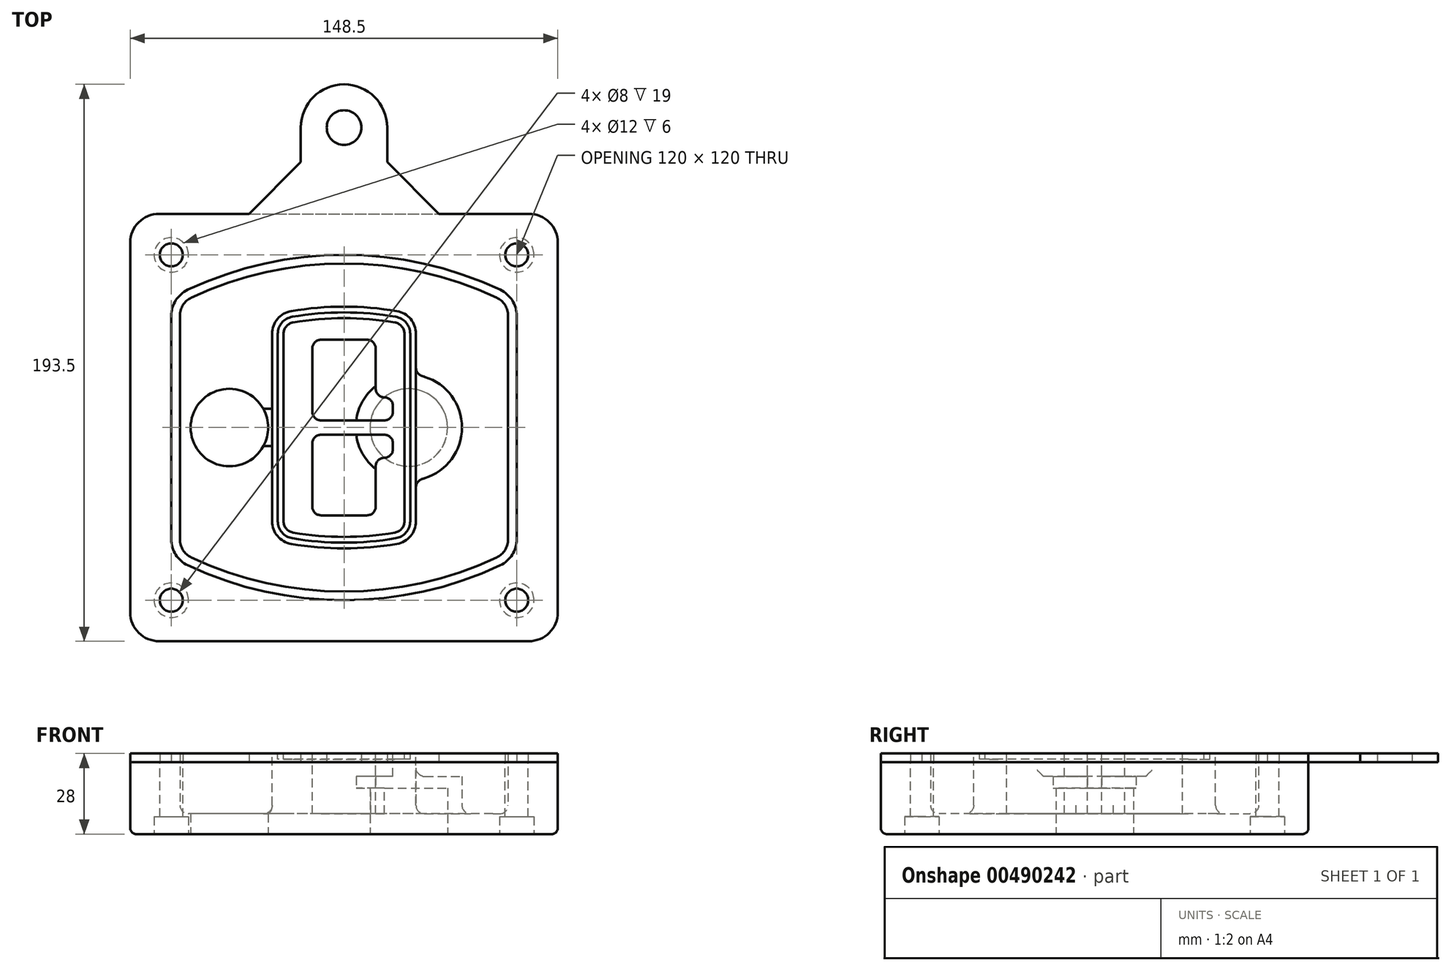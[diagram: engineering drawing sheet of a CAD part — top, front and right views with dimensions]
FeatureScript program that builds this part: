
annotation { "Feature Type Name" : "Feature", "Feature Type Description" : "" }
export const myFeature = defineFeature(function(context is Context, id is Id, definition is map)
    precondition{}
    {
        {
            var Q0;
            Q0=qCreatedBy(makeId("Top.planeOp"),FACE);
            var sketch = newSketch(context, id + "F0", { "sketchPlane" : qUnion([Q0])});
            skPoint(sketch, "E0.rect.middle", {"position": v(0, 0) * mm});
            skLineSegment(sketch, "E1.bottom", {"start": v(-64.25, -74.25) * mm, "end": v(64.25, -74.25) * mm});
            skLineSegment(sketch, "E1.top", {"start": v(-64.25, 74.25) * mm, "end": v(64.25, 74.25) * mm});
            skLineSegment(sketch, "E1.left", {"start": v(-74.25, -64.25) * mm, "end": v(-74.25, 64.25) * mm});
            skLineSegment(sketch, "E1.right", {"start": v(74.25, -64.25) * mm, "end": v(74.25, 64.25) * mm});
            skLineSegment(sketch, "E2", {"start": v(-74.25, 74.25) * mm, "end": v(74.25, -74.25) * mm, "construction": true});
            skLineSegment(sketch, "E3", {"start": v(74.25, 74.25) * mm, "end": v(-74.25, -74.25) * mm, "construction": true});
            skCircle(sketch, "E4", {"center": v(-60, 60) * mm, "radius": 4 * mm});
            skCircle(sketch, "E5", {"center": v(60, 60) * mm, "radius": 4 * mm});
            skCircle(sketch, "E6", {"center": v(60, -60) * mm, "radius": 4 * mm});
            skCircle(sketch, "E7", {"center": v(-60, -60) * mm, "radius": 4 * mm});
            skLineSegment(sketch, "E8", {"start": v(-60, 60) * mm, "end": v(60, 60) * mm, "construction": true});
            skLineSegment(sketch, "E9", {"start": v(60, 60) * mm, "end": v(60, -60) * mm, "construction": true});
            skLineSegment(sketch, "E10", {"start": v(60, -60) * mm, "end": v(-60, -60) * mm, "construction": true});
            skLineSegment(sketch, "E11", {"start": v(-60, -60) * mm, "end": v(-60, 60) * mm, "construction": true});
            skLineSegment(sketch, "E12", {"start": v(-60, 38.83) * mm, "end": v(-60, -38.83) * mm});
            skLineSegment(sketch, "E13", {"start": v(60, 38.83) * mm, "end": v(60, -38.83) * mm});
            skArc(sketch, "E14", {"start": v(54.26, 47.88) * mm, "mid": v(0, 60) * mm, "end": v(-54.26, 47.88) * mm});
            skArc(sketch, "E15", {"start": v(-54.26, -47.88) * mm, "mid": v(0, -60) * mm, "end": v(54.26, -47.88) * mm});
            skLineSegment(sketch, "E16", {"start": v(-60, 0) * mm, "end": v(60, 0) * mm, "construction": true});
            skPoint(sketch, "E17.visualSharp", {"position": v(-60, -45) * mm});
            skArc(sketch, "E17.filletArc", {"start": v(-60, -38.83) * mm, "mid": v(-58.44, -44.2) * mm, "end": v(-54.26, -47.88) * mm});
            skPoint(sketch, "E18.visualSharp", {"position": v(-60, 45) * mm});
            skArc(sketch, "E18.filletArc", {"start": v(-54.26, 47.88) * mm, "mid": v(-58.44, 44.2) * mm, "end": v(-60, 38.83) * mm});
            skPoint(sketch, "E19.visualSharp", {"position": v(60, 45) * mm});
            skArc(sketch, "E19.filletArc", {"start": v(60, 38.83) * mm, "mid": v(58.44, 44.2) * mm, "end": v(54.26, 47.88) * mm});
            skPoint(sketch, "E20.visualSharp", {"position": v(60, -45) * mm});
            skArc(sketch, "E20.filletArc", {"start": v(54.26, -47.88) * mm, "mid": v(58.44, -44.2) * mm, "end": v(60, -38.83) * mm});
            skPoint(sketch, "E21.visualSharp", {"position": v(-74.25, 74.25) * mm});
            skArc(sketch, "E21.filletArc", {"start": v(-64.25, 74.25) * mm, "mid": v(-71.32, 71.32) * mm, "end": v(-74.25, 64.25) * mm});
            skPoint(sketch, "E22.visualSharp", {"position": v(74.25, 74.25) * mm});
            skArc(sketch, "E22.filletArc", {"start": v(74.25, 64.25) * mm, "mid": v(71.32, 71.32) * mm, "end": v(64.25, 74.25) * mm});
            skPoint(sketch, "E23.visualSharp", {"position": v(74.25, -74.25) * mm});
            skArc(sketch, "E23.filletArc", {"start": v(64.25, -74.25) * mm, "mid": v(71.32, -71.32) * mm, "end": v(74.25, -64.25) * mm});
            skPoint(sketch, "E24.visualSharp", {"position": v(-74.25, -74.25) * mm});
            skArc(sketch, "E24.filletArc", {"start": v(-74.25, -64.25) * mm, "mid": v(-71.32, -71.32) * mm, "end": v(-64.25, -74.25) * mm});
            skArc(sketch, "E25.0", {"start": v(57, 38.83) * mm, "mid": v(55.9, 42.58) * mm, "end": v(52.98, 45.17) * mm});
            skLineSegment(sketch, "E25.1", {"start": v(57, 38.83) * mm, "end": v(57, -38.83) * mm});
            skArc(sketch, "E25.2", {"start": v(52.98, -45.17) * mm, "mid": v(55.9, -42.58) * mm, "end": v(57, -38.83) * mm});
            skArc(sketch, "E25.3", {"start": v(-52.98, -45.17) * mm, "mid": v(0, -57) * mm, "end": v(52.98, -45.17) * mm});
            skArc(sketch, "E25.4", {"start": v(-57, -38.83) * mm, "mid": v(-55.9, -42.58) * mm, "end": v(-52.98, -45.17) * mm});
            skArc(sketch, "E25.5", {"start": v(52.98, 45.17) * mm, "mid": v(0, 57) * mm, "end": v(-52.98, 45.17) * mm});
            skLineSegment(sketch, "E25.6", {"start": v(-57, 38.83) * mm, "end": v(-57, -38.83) * mm});
            skArc(sketch, "E25.7", {"start": v(-52.98, 45.17) * mm, "mid": v(-55.9, 42.58) * mm, "end": v(-57, 38.83) * mm});
            skArc(sketch, "E26.0", {"start": v(-55.96, 51.5) * mm, "mid": v(-61.82, 46.33) * mm, "end": v(-64, 38.83) * mm});
            skArc(sketch, "E26.1", {"start": v(55.96, 51.5) * mm, "mid": v(0, 64) * mm, "end": v(-55.96, 51.5) * mm});
            skArc(sketch, "E26.2", {"start": v(64, 38.83) * mm, "mid": v(61.82, 46.33) * mm, "end": v(55.96, 51.5) * mm});
            skLineSegment(sketch, "E26.3", {"start": v(64, 38.83) * mm, "end": v(64, -38.83) * mm});
            skArc(sketch, "E26.4", {"start": v(55.96, -51.5) * mm, "mid": v(61.82, -46.33) * mm, "end": v(64, -38.83) * mm});
            skLineSegment(sketch, "E26.5", {"start": v(-64, 38.83) * mm, "end": v(-64, -38.83) * mm});
            skArc(sketch, "E26.6", {"start": v(-55.96, -51.5) * mm, "mid": v(0, -64) * mm, "end": v(55.96, -51.5) * mm});
            skArc(sketch, "E26.7", {"start": v(-64, -38.83) * mm, "mid": v(-61.82, -46.33) * mm, "end": v(-55.96, -51.5) * mm});
            skSolve(sketch);
        }
        {
            var Q0;
            Q0=makeQuery(id+"F0.imprint","IMPRINT",FACE,{"disambiguationData":[TD([[makeQuery(id+"F0.imprint","IMPRINT",EDGE,{"derivedFrom":sQuery(id+"F0.wireOp",EDGE,"E1.bottom")}),1.0]])]});
            var Q1;
            Q1=makeQuery(id+"F0.imprint","IMPRINT",FACE,{"disambiguationData":[TD([[makeQuery(id+"F0.imprint","IMPRINT",EDGE,{"derivedFrom":sQuery(id+"F0.wireOp",EDGE,"E12")}),1.0]])]});
            var Q2;
            Q2=makeQuery(id+"F0.imprint","IMPRINT",FACE,{"disambiguationData":[TD([[makeQuery(id+"F0.imprint","IMPRINT",EDGE,{"derivedFrom":sQuery(id+"F0.wireOp",EDGE,"E25.0")}),1.0]])]});
            var Q3;
            Q3=makeQuery(id+"F0.imprint","IMPRINT",FACE,{"disambiguationData":[TD([[makeQuery(id+"F0.imprint","IMPRINT",EDGE,{"derivedFrom":sQuery(id+"F0.wireOp",EDGE,"E12")}),-1.0]])]});
            extrude(context, id + "F1", {"entities" : qUnion([Q0, Q1, Q2, Q3]), "oppositeDirection" : true, "depth" : 25 * mm});
        }
        {
            var Q0;
            Q0=makeQuery(id+"F0.imprint","IMPRINT",FACE,{"disambiguationData":[TD([[makeQuery(id+"F0.imprint","IMPRINT",EDGE,{"derivedFrom":sQuery(id+"F0.wireOp",EDGE,"E12")}),1.0]])]});
            extrude(context, id + "F2", {"entities" : qUnion([Q0]), "operationType" : NewBodyOperationType.ADD, "depth" : 3 * mm});
        }
        {
            var Q0;
            Q0=makeQuery(id+"F0.imprint","IMPRINT",FACE,{"disambiguationData":[TD([[makeQuery(id+"F0.imprint","IMPRINT",EDGE,{"derivedFrom":sQuery(id+"F0.wireOp",EDGE,"E25.0")}),1.0]])]});
            extrude(context, id + "F3", {"entities" : qUnion([Q0]), "operationType" : NewBodyOperationType.REMOVE, "oppositeDirection" : true, "depth" : 18 * mm});
        }
        {
            var Q0;
            Q0=makeQuery(id+"F2.opExtrude","CAP_FACE",FACE,{"disambiguationData":[OSD([sQuery(id+"F0.wireOp",EDGE,"E12"),sQuery(id+"F0.wireOp",EDGE,"E13"),sQuery(id+"F0.wireOp",EDGE,"E14"),sQuery(id+"F0.wireOp",EDGE,"E15"),sQuery(id+"F0.wireOp",EDGE,"E17.filletArc"),sQuery(id+"F0.wireOp",EDGE,"E18.filletArc"),sQuery(id+"F0.wireOp",EDGE,"E19.filletArc"),sQuery(id+"F0.wireOp",EDGE,"E20.filletArc"),sQuery(id+"F0.wireOp",EDGE,"E25.0"),sQuery(id+"F0.wireOp",EDGE,"E25.1"),sQuery(id+"F0.wireOp",EDGE,"E25.2"),sQuery(id+"F0.wireOp",EDGE,"E25.3"),sQuery(id+"F0.wireOp",EDGE,"E25.4"),sQuery(id+"F0.wireOp",EDGE,"E25.5"),sQuery(id+"F0.wireOp",EDGE,"E25.6"),sQuery(id+"F0.wireOp",EDGE,"E25.7")])],"isStart":false});
            var sketch = newSketch(context, id + "F4", { "sketchPlane" : qUnion([Q0])});
            skArc(sketch, "E27.0", {"start": v(-18.34, -40.45) * mm, "mid": v(0, -42) * mm, "end": v(18.34, -40.45) * mm});
            skArc(sketch, "E28.0", {"start": v(18.34, 40.45) * mm, "mid": v(0, 42) * mm, "end": v(-18.34, 40.45) * mm});
            skLineSegment(sketch, "E29", {"start": v(-25, 32.57) * mm, "end": v(-25, -32.57) * mm});
            skLineSegment(sketch, "E30", {"start": v(25, 32.57) * mm, "end": v(25, -32.57) * mm});
            skLineSegment(sketch, "E31", {"start": v(-25, 39.1) * mm, "end": v(25, 39.1) * mm, "construction": true});
            skLineSegment(sketch, "E32", {"start": v(-25, -39.1) * mm, "end": v(25, -39.1) * mm, "construction": true});
            skPoint(sketch, "E33.visualSharp", {"position": v(-25, 39.1) * mm});
            skArc(sketch, "E33.filletArc", {"start": v(-18.34, 40.45) * mm, "mid": v(-23.11, 37.73) * mm, "end": v(-25, 32.57) * mm});
            skPoint(sketch, "E34.visualSharp", {"position": v(25, 39.1) * mm});
            skArc(sketch, "E34.filletArc", {"start": v(25, 32.57) * mm, "mid": v(23.11, 37.73) * mm, "end": v(18.34, 40.45) * mm});
            skPoint(sketch, "E35.visualSharp", {"position": v(25, -39.1) * mm});
            skArc(sketch, "E35.filletArc", {"start": v(18.34, -40.45) * mm, "mid": v(23.11, -37.73) * mm, "end": v(25, -32.57) * mm});
            skPoint(sketch, "E36.visualSharp", {"position": v(-25, -39.1) * mm});
            skArc(sketch, "E36.filletArc", {"start": v(-25, -32.57) * mm, "mid": v(-23.11, -37.73) * mm, "end": v(-18.34, -40.45) * mm});
            skArc(sketch, "E37.0", {"start": v(52.98, 45.17) * mm, "mid": v(0, 57) * mm, "end": v(-52.98, 45.17) * mm});
            skArc(sketch, "E37.1", {"start": v(-52.98, 45.17) * mm, "mid": v(-55.9, 42.58) * mm, "end": v(-57, 38.83) * mm});
            skLineSegment(sketch, "E37.2", {"start": v(-57, 38.83) * mm, "end": v(-57, -38.83) * mm});
            skArc(sketch, "E37.3", {"start": v(-57, -38.83) * mm, "mid": v(-55.9, -42.58) * mm, "end": v(-52.98, -45.17) * mm});
            skArc(sketch, "E37.4", {"start": v(-52.98, -45.17) * mm, "mid": v(0, -57) * mm, "end": v(52.98, -45.17) * mm});
            skArc(sketch, "E37.5", {"start": v(52.98, -45.17) * mm, "mid": v(55.9, -42.58) * mm, "end": v(57, -38.83) * mm});
            skLineSegment(sketch, "E37.6", {"start": v(57, 38.83) * mm, "end": v(57, -38.83) * mm});
            skArc(sketch, "E37.7", {"start": v(57, 38.83) * mm, "mid": v(55.9, 42.58) * mm, "end": v(52.98, 45.17) * mm});
            skLineSegment(sketch, "E38.0", {"start": v(23, 32.57) * mm, "end": v(23, -32.57) * mm});
            skArc(sketch, "E38.1", {"start": v(18, -38.48) * mm, "mid": v(21.58, -36.44) * mm, "end": v(23, -32.57) * mm});
            skArc(sketch, "E38.2", {"start": v(-18, -38.48) * mm, "mid": v(0, -40) * mm, "end": v(18, -38.48) * mm});
            skArc(sketch, "E38.3", {"start": v(-23, -32.57) * mm, "mid": v(-21.58, -36.44) * mm, "end": v(-18, -38.48) * mm});
            skLineSegment(sketch, "E38.4", {"start": v(-23, 32.57) * mm, "end": v(-23, -32.57) * mm});
            skArc(sketch, "E38.5", {"start": v(23, 32.57) * mm, "mid": v(21.58, 36.44) * mm, "end": v(18, 38.48) * mm});
            skArc(sketch, "E38.6", {"start": v(-18, 38.48) * mm, "mid": v(-21.58, 36.44) * mm, "end": v(-23, 32.57) * mm});
            skArc(sketch, "E38.7", {"start": v(18, 38.48) * mm, "mid": v(0, 40) * mm, "end": v(-18, 38.48) * mm});
            skArc(sketch, "E39.0", {"start": v(21, 32.57) * mm, "mid": v(20.06, 35.15) * mm, "end": v(17.67, 36.5) * mm});
            skLineSegment(sketch, "E39.1", {"start": v(21, 32.57) * mm, "end": v(21, -32.57) * mm});
            skArc(sketch, "E39.2", {"start": v(17.67, -36.5) * mm, "mid": v(20.06, -35.15) * mm, "end": v(21, -32.57) * mm});
            skArc(sketch, "E39.3", {"start": v(-17.67, -36.5) * mm, "mid": v(0, -38) * mm, "end": v(17.67, -36.5) * mm});
            skArc(sketch, "E39.4", {"start": v(-21, -32.57) * mm, "mid": v(-20.06, -35.15) * mm, "end": v(-17.67, -36.5) * mm});
            skArc(sketch, "E39.5", {"start": v(17.67, 36.5) * mm, "mid": v(0, 38) * mm, "end": v(-17.67, 36.5) * mm});
            skLineSegment(sketch, "E39.6", {"start": v(-21, 32.57) * mm, "end": v(-21, -32.57) * mm});
            skArc(sketch, "E39.7", {"start": v(-17.67, 36.5) * mm, "mid": v(-20.06, 35.15) * mm, "end": v(-21, 32.57) * mm});
            skLineSegment(sketch, "E40", {"start": v(-25, 0) * mm, "end": v(25, 0) * mm, "construction": true});
            skLineSegment(sketch, "E41", {"start": v(-11, 5.5) * mm, "end": v(-11, 27.5) * mm});
            skLineSegment(sketch, "E42", {"start": v(-8, 30.5) * mm, "end": v(8, 30.5) * mm});
            skLineSegment(sketch, "E43", {"start": v(11, 27.5) * mm, "end": v(11, 13.5) * mm});
            skLineSegment(sketch, "E44", {"start": v(14, 10.5) * mm, "end": v(14, 10.5) * mm});
            skLineSegment(sketch, "E45", {"start": v(17, 7.5) * mm, "end": v(17, 5.5) * mm});
            skLineSegment(sketch, "E46", {"start": v(14, 2.5) * mm, "end": v(-8, 2.5) * mm});
            skPoint(sketch, "E47.visualSharp", {"position": v(-11, 30.5) * mm});
            skArc(sketch, "E47.filletArc", {"start": v(-8, 30.5) * mm, "mid": v(-10.12, 29.62) * mm, "end": v(-11, 27.5) * mm});
            skPoint(sketch, "E48.visualSharp", {"position": v(11, 30.5) * mm});
            skArc(sketch, "E48.filletArc", {"start": v(11, 27.5) * mm, "mid": v(10.12, 29.62) * mm, "end": v(8, 30.5) * mm});
            skPoint(sketch, "E49.visualSharp", {"position": v(11, 10.5) * mm});
            skArc(sketch, "E49.filletArc", {"start": v(11, 13.5) * mm, "mid": v(11.88, 11.38) * mm, "end": v(14, 10.5) * mm});
            skPoint(sketch, "E50.visualSharp", {"position": v(17, 10.5) * mm});
            skArc(sketch, "E50.filletArc", {"start": v(17, 7.5) * mm, "mid": v(16.12, 9.62) * mm, "end": v(14, 10.5) * mm});
            skPoint(sketch, "E51.visualSharp", {"position": v(17, 2.5) * mm});
            skArc(sketch, "E51.filletArc", {"start": v(14, 2.5) * mm, "mid": v(16.12, 3.38) * mm, "end": v(17, 5.5) * mm});
            skPoint(sketch, "E52.visualSharp", {"position": v(-11, 2.5) * mm});
            skArc(sketch, "E52.filletArc", {"start": v(-11, 5.5) * mm, "mid": v(-10.12, 3.38) * mm, "end": v(-8, 2.5) * mm});
            skLineSegment(sketch, "E53.0.MirrorCS", {"start": v(14, -2.5) * mm, "end": v(-8, -2.5) * mm});
            skArc(sketch, "E54.0.MirrorCS", {"start": v(-11, -5.5) * mm, "mid": v(-10.12, -3.38) * mm, "end": v(-8, -2.5) * mm});
            skLineSegment(sketch, "E55.0.MirrorCS", {"start": v(-11, -5.5) * mm, "end": v(-11, -27.5) * mm});
            skArc(sketch, "E56.0.MirrorCS", {"start": v(-8, -30.5) * mm, "mid": v(-10.12, -29.62) * mm, "end": v(-11, -27.5) * mm});
            skLineSegment(sketch, "E57.0.MirrorCS", {"start": v(-8, -30.5) * mm, "end": v(8, -30.5) * mm});
            skArc(sketch, "E58.0.MirrorCS", {"start": v(11, -27.5) * mm, "mid": v(10.12, -29.62) * mm, "end": v(8, -30.5) * mm});
            skLineSegment(sketch, "E59.0.MirrorCS", {"start": v(11, -27.5) * mm, "end": v(11, -13.5) * mm});
            skArc(sketch, "E60.0.MirrorCS", {"start": v(11, -13.5) * mm, "mid": v(11.88, -11.38) * mm, "end": v(14, -10.5) * mm});
            skArc(sketch, "E61.0.MirrorCS", {"start": v(17, -7.5) * mm, "mid": v(16.12, -9.62) * mm, "end": v(14, -10.5) * mm});
            skLineSegment(sketch, "E62.0.MirrorCS", {"start": v(17, -7.5) * mm, "end": v(17, -5.5) * mm});
            skArc(sketch, "E63.0.MirrorCS", {"start": v(14, -2.5) * mm, "mid": v(16.12, -3.38) * mm, "end": v(17, -5.5) * mm});
            skSolve(sketch);
        }
        {
            var Q0;
            Q0=makeQuery(id+"F4.imprint","IMPRINT",FACE,{"disambiguationData":[TD([[makeQuery(id+"F4.imprint","IMPRINT",EDGE,{"derivedFrom":sQuery(id+"F4.wireOp",EDGE,"E27.0")}),1.0]])]});
            var Q1;
            Q1=makeQuery(id+"F4.imprint","IMPRINT",FACE,{"disambiguationData":[TD([[makeQuery(id+"F4.imprint","IMPRINT",EDGE,{"derivedFrom":sQuery(id+"F4.wireOp",EDGE,"E38.0")}),-1.0]])]});
            var Q2;
            Q2=makeQuery(id+"F4.imprint","IMPRINT",FACE,{"disambiguationData":[TD([[makeQuery(id+"F4.imprint","IMPRINT",EDGE,{"derivedFrom":sQuery(id+"F4.wireOp",EDGE,"E39.0")}),1.0]])]});
            extrude(context, id + "F5", {"entities" : qUnion([Q0, Q1, Q2]), "operationType" : NewBodyOperationType.ADD, "endBound" : BoundingType.UP_TO_NEXT, "oppositeDirection" : true, "depth" : 25 * mm});
        }
        {
            var Q0;
            Q0=makeQuery(id+"F4.imprint","IMPRINT",FACE,{"disambiguationData":[TD([[makeQuery(id+"F4.imprint","IMPRINT",EDGE,{"derivedFrom":sQuery(id+"F4.wireOp",EDGE,"E38.0")}),-1.0]])]});
            extrude(context, id + "F6", {"entities" : qUnion([Q0]), "operationType" : NewBodyOperationType.REMOVE, "oppositeDirection" : true, "depth" : 2 * mm});
        }
        {
            var Q0;
            Q0=makeQuery(id+"F1.opExtrude","CAP_FACE",FACE,{"disambiguationData":[OSD([sQuery(id+"F0.wireOp",EDGE,"E1.bottom"),sQuery(id+"F0.wireOp",EDGE,"E1.top"),sQuery(id+"F0.wireOp",EDGE,"E1.left"),sQuery(id+"F0.wireOp",EDGE,"E1.right"),sQuery(id+"F0.wireOp",EDGE,"E4"),sQuery(id+"F0.wireOp",EDGE,"E5"),sQuery(id+"F0.wireOp",EDGE,"E6"),sQuery(id+"F0.wireOp",EDGE,"E7"),sQuery(id+"F0.wireOp",EDGE,"E21.filletArc"),sQuery(id+"F0.wireOp",EDGE,"E22.filletArc"),sQuery(id+"F0.wireOp",EDGE,"E23.filletArc"),sQuery(id+"F0.wireOp",EDGE,"E24.filletArc")])],"isStart":false});
            var sketch = newSketch(context, id + "F7", { "sketchPlane" : qUnion([Q0])});
            skCircle(sketch, "E64", {"center": v(22.5, 0) * mm, "radius": 13.47 * mm});
            skCircle(sketch, "E65", {"center": v(-39.81, 0) * mm, "radius": 13.47 * mm});
            skLineSegment(sketch, "E66", {"start": v(74.25, 0) * mm, "end": v(-74.25, 0) * mm});
            skCircle(sketch, "E67", {"center": v(22.5, 0) * mm, "radius": 18.47 * mm});
            skCircle(sketch, "E68", {"center": v(60, -60) * mm, "radius": 6 * mm});
            skCircle(sketch, "E69", {"center": v(-60, -60) * mm, "radius": 6 * mm});
            skCircle(sketch, "E70", {"center": v(-60, 60) * mm, "radius": 6 * mm});
            skCircle(sketch, "E71", {"center": v(60, 60) * mm, "radius": 6 * mm});
            skSolve(sketch);
        }
        {
            var Q0;
            {var subQ1=sQuery(id+"F7.wireOp",EDGE,"E66");var subQ4=sQuery(id+"F7.wireOp",EDGE,"E64");var subQ6=makeQuery(id+"F7.imprint","INTERSECT",VERTEX,{"disambiguationData":[OD(0.0)],"derivedFrom":[subQ4,subQ1]});Q0=makeQuery(id+"F7.imprint","IMPRINT",FACE,{"disambiguationData":[TD([[makeQuery(id+"F7.imprint","IMPRINT",EDGE,{"disambiguationData":[TD([[subQ6,-1.0]])],"derivedFrom":subQ4}),-1.0]])]});}
            var Q1;
            {var subQ0=sQuery(id+"F7.wireOp",EDGE,"E66");var subQ1=sQuery(id+"F7.wireOp",EDGE,"E64");var subQ3=makeQuery(id+"F7.imprint","INTERSECT",VERTEX,{"disambiguationData":[OD(0.0)],"derivedFrom":[subQ1,subQ0]});Q1=makeQuery(id+"F7.imprint","IMPRINT",FACE,{"disambiguationData":[TD([[makeQuery(id+"F7.imprint","IMPRINT",EDGE,{"disambiguationData":[TD([[subQ3,-1.0]])],"derivedFrom":subQ1}),1.0]])]});}
            var Q2;
            {var subQ0=sQuery(id+"F7.wireOp",EDGE,"E66");var subQ1=sQuery(id+"F7.wireOp",EDGE,"E64");var subQ3=makeQuery(id+"F7.imprint","INTERSECT",VERTEX,{"disambiguationData":[OD(0.0)],"derivedFrom":[subQ1,subQ0]});Q2=makeQuery(id+"F7.imprint","IMPRINT",FACE,{"disambiguationData":[TD([[makeQuery(id+"F7.imprint","IMPRINT",EDGE,{"disambiguationData":[TD([[subQ3,1.0]])],"derivedFrom":subQ1}),1.0]])]});}
            var Q3;
            {var subQ1=sQuery(id+"F7.wireOp",EDGE,"E66");var subQ4=sQuery(id+"F7.wireOp",EDGE,"E64");var subQ6=makeQuery(id+"F7.imprint","INTERSECT",VERTEX,{"disambiguationData":[OD(0.0)],"derivedFrom":[subQ4,subQ1]});Q3=makeQuery(id+"F7.imprint","IMPRINT",FACE,{"disambiguationData":[TD([[makeQuery(id+"F7.imprint","IMPRINT",EDGE,{"disambiguationData":[TD([[subQ6,1.0]])],"derivedFrom":subQ4}),-1.0]])]});}
            extrude(context, id + "F8", {"entities" : qUnion([Q0, Q1, Q2, Q3]), "operationType" : NewBodyOperationType.ADD, "oppositeDirection" : true, "depth" : 20 * mm});
        }
        {
            var Q0;
            {var subQ0=sQuery(id+"F7.wireOp",EDGE,"E66");var subQ1=sQuery(id+"F7.wireOp",EDGE,"E64");var subQ3=makeQuery(id+"F7.imprint","INTERSECT",VERTEX,{"disambiguationData":[OD(0.0)],"derivedFrom":[subQ1,subQ0]});Q0=makeQuery(id+"F7.imprint","IMPRINT",FACE,{"disambiguationData":[TD([[makeQuery(id+"F7.imprint","IMPRINT",EDGE,{"disambiguationData":[TD([[subQ3,-1.0]])],"derivedFrom":subQ1}),1.0]])]});}
            var Q1;
            {var subQ0=sQuery(id+"F7.wireOp",EDGE,"E66");var subQ1=sQuery(id+"F7.wireOp",EDGE,"E64");var subQ3=makeQuery(id+"F7.imprint","INTERSECT",VERTEX,{"disambiguationData":[OD(0.0)],"derivedFrom":[subQ1,subQ0]});Q1=makeQuery(id+"F7.imprint","IMPRINT",FACE,{"disambiguationData":[TD([[makeQuery(id+"F7.imprint","IMPRINT",EDGE,{"disambiguationData":[TD([[subQ3,1.0]])],"derivedFrom":subQ1}),1.0]])]});}
            extrude(context, id + "F9", {"entities" : qUnion([Q0, Q1]), "operationType" : NewBodyOperationType.REMOVE, "oppositeDirection" : true, "depth" : 16 * mm});
        }
        {
            var Q0;
            {var subQ0=sQuery(id+"F7.wireOp",EDGE,"E66");var subQ1=sQuery(id+"F7.wireOp",EDGE,"E65");var subQ3=makeQuery(id+"F7.imprint","INTERSECT",VERTEX,{"disambiguationData":[OD(0.0)],"derivedFrom":[subQ1,subQ0]});Q0=makeQuery(id+"F7.imprint","IMPRINT",FACE,{"disambiguationData":[TD([[makeQuery(id+"F7.imprint","IMPRINT",EDGE,{"disambiguationData":[TD([[subQ3,-1.0]])],"derivedFrom":subQ1}),1.0]])]});}
            var Q1;
            {var subQ0=sQuery(id+"F7.wireOp",EDGE,"E66");var subQ1=sQuery(id+"F7.wireOp",EDGE,"E65");var subQ3=makeQuery(id+"F7.imprint","INTERSECT",VERTEX,{"disambiguationData":[OD(0.0)],"derivedFrom":[subQ1,subQ0]});Q1=makeQuery(id+"F7.imprint","IMPRINT",FACE,{"disambiguationData":[TD([[makeQuery(id+"F7.imprint","IMPRINT",EDGE,{"disambiguationData":[TD([[subQ3,1.0]])],"derivedFrom":subQ1}),1.0]])]});}
            extrude(context, id + "F10", {"entities" : qUnion([Q0, Q1]), "operationType" : NewBodyOperationType.REMOVE, "oppositeDirection" : true, "depth" : 25 * mm});
        }
        {
            var Q0;
            Q0=makeQuery(id+"F7.imprint","IMPRINT",FACE,{"disambiguationData":[TD([[makeQuery(id+"F7.imprint","IMPRINT",EDGE,{"derivedFrom":sQuery(id+"F7.wireOp",EDGE,"E68")}),1.0]])]});
            var Q1;
            Q1=makeQuery(id+"F7.imprint","IMPRINT",FACE,{"disambiguationData":[TD([[makeQuery(id+"F7.imprint","IMPRINT",EDGE,{"derivedFrom":makeQuery(id+"F1.opExtrude","CAP_EDGE",EDGE,{"disambiguationData":[OSD([sQuery(id+"F0.wireOp",EDGE,"E5")])],"isStart":false})}),-1.0]])]});
            var Q2;
            Q2=makeQuery(id+"F7.imprint","IMPRINT",FACE,{"disambiguationData":[TD([[makeQuery(id+"F7.imprint","IMPRINT",EDGE,{"derivedFrom":sQuery(id+"F7.wireOp",EDGE,"E69")}),1.0]])]});
            var Q3;
            Q3=makeQuery(id+"F7.imprint","IMPRINT",FACE,{"disambiguationData":[TD([[makeQuery(id+"F7.imprint","IMPRINT",EDGE,{"derivedFrom":makeQuery(id+"F1.opExtrude","CAP_EDGE",EDGE,{"disambiguationData":[OSD([sQuery(id+"F0.wireOp",EDGE,"E4")])],"isStart":false})}),-1.0]])]});
            var Q4;
            Q4=makeQuery(id+"F7.imprint","IMPRINT",FACE,{"disambiguationData":[TD([[makeQuery(id+"F7.imprint","IMPRINT",EDGE,{"derivedFrom":sQuery(id+"F7.wireOp",EDGE,"E70")}),1.0]])]});
            var Q5;
            Q5=makeQuery(id+"F7.imprint","IMPRINT",FACE,{"disambiguationData":[TD([[makeQuery(id+"F7.imprint","IMPRINT",EDGE,{"derivedFrom":makeQuery(id+"F1.opExtrude","CAP_EDGE",EDGE,{"disambiguationData":[OSD([sQuery(id+"F0.wireOp",EDGE,"E7")])],"isStart":false})}),-1.0]])]});
            var Q6;
            Q6=makeQuery(id+"F7.imprint","IMPRINT",FACE,{"disambiguationData":[TD([[makeQuery(id+"F7.imprint","IMPRINT",EDGE,{"derivedFrom":sQuery(id+"F7.wireOp",EDGE,"E71")}),1.0]])]});
            var Q7;
            Q7=makeQuery(id+"F7.imprint","IMPRINT",FACE,{"disambiguationData":[TD([[makeQuery(id+"F7.imprint","IMPRINT",EDGE,{"derivedFrom":makeQuery(id+"F1.opExtrude","CAP_EDGE",EDGE,{"disambiguationData":[OSD([sQuery(id+"F0.wireOp",EDGE,"E6")])],"isStart":false})}),-1.0]])]});
            extrude(context, id + "F11", {"entities" : qUnion([Q0, Q1, Q2, Q3, Q4, Q5, Q6, Q7]), "operationType" : NewBodyOperationType.REMOVE, "oppositeDirection" : true, "depth" : 6 * mm});
        }
        {
            var Q0;
            Q0=makeQuery(id+"F9.boolean.opBoolean","COPY",FACE,{"derivedFrom":makeQuery(id+"F9.opExtrude","CAP_FACE",FACE,{"disambiguationData":[OSD([sQuery(id+"F7.wireOp",EDGE,"E64")])],"isStart":false})});
            var sketch = newSketch(context, id + "F12", { "sketchPlane" : qUnion([Q0])});
            skArc(sketch, "E72.0", {"start": v(11, 14.45) * mm, "mid": v(6.45, 9.13) * mm, "end": v(4.2, 2.5) * mm});
            skArc(sketch, "E72.1", {"start": v(4.2, -2.5) * mm, "mid": v(6.45, -9.13) * mm, "end": v(11, -14.45) * mm});
            skLineSegment(sketch, "E73", {"start": v(4.2, -2.5) * mm, "end": v(14, -2.5) * mm});
            skLineSegment(sketch, "E74.0", {"start": v(14, 2.5) * mm, "end": v(4.2, 2.5) * mm});
            skArc(sketch, "E74.1", {"start": v(14, 2.5) * mm, "mid": v(16.12, 3.38) * mm, "end": v(17, 5.5) * mm});
            skLineSegment(sketch, "E74.2", {"start": v(17, 7.5) * mm, "end": v(17, 5.5) * mm});
            skArc(sketch, "E74.3", {"start": v(17, 7.5) * mm, "mid": v(16.12, 9.62) * mm, "end": v(14, 10.5) * mm});
            skArc(sketch, "E74.4", {"start": v(11, 13.5) * mm, "mid": v(11.88, 11.38) * mm, "end": v(14, 10.5) * mm});
            skLineSegment(sketch, "E74.5", {"start": v(11, 14.45) * mm, "end": v(11, 13.5) * mm});
            skLineSegment(sketch, "E74.7", {"start": v(14, -2.5) * mm, "end": v(4.2, -2.5) * mm});
            skArc(sketch, "E74.8", {"start": v(14, -2.5) * mm, "mid": v(16.12, -3.38) * mm, "end": v(17, -5.5) * mm});
            skLineSegment(sketch, "E74.9", {"start": v(17, -7.5) * mm, "end": v(17, -5.5) * mm});
            skArc(sketch, "E74.10", {"start": v(17, -7.5) * mm, "mid": v(16.12, -9.62) * mm, "end": v(14, -10.5) * mm});
            skArc(sketch, "E74.11", {"start": v(11, -13.5) * mm, "mid": v(11.88, -11.38) * mm, "end": v(14, -10.5) * mm});
            skLineSegment(sketch, "E74.12", {"start": v(11, -14.45) * mm, "end": v(11, -13.5) * mm});
            skPoint(sketch, "E75.orphan", {"position": v(11, -27.5) * mm});
            skPoint(sketch, "E76.orphan", {"position": v(-8, -2.5) * mm});
            skPoint(sketch, "E77.orphan", {"position": v(-8, 2.5) * mm});
            skPoint(sketch, "E78.orphan", {"position": v(11, 27.5) * mm});
            skSolve(sketch);
        }
        {
            var Q0;
            {var subQ7=sQuery(id+"F12.wireOp",EDGE,"E72.0");var subQ14=sQuery(id+"F12.wireOp",EDGE,"E72.1");var subQ16=sQuery(id+"F12.wireOp",EDGE,"E74.1");var subQ18=sQuery(id+"F12.wireOp",EDGE,"E74.8");Q0=qUnion([makeQuery(id+"F12.imprint","IMPRINT",FACE,{"disambiguationData":[TD([[makeQuery(id+"F12.imprint","IMPRINT",EDGE,{"derivedFrom":subQ7}),1.0]])]}),makeQuery(id+"F12.imprint","IMPRINT",FACE,{"disambiguationData":[TD([[makeQuery(id+"F12.imprint","IMPRINT",EDGE,{"derivedFrom":subQ14}),1.0]])]}),makeQuery(id+"F12.imprint","IMPRINT",FACE,{"disambiguationData":[TD([[makeQuery(id+"F12.imprint","IMPRINT",EDGE,{"derivedFrom":subQ16}),1.0]])]}),makeQuery(id+"F12.imprint","IMPRINT",FACE,{"disambiguationData":[TD([[makeQuery(id+"F12.imprint","IMPRINT",EDGE,{"derivedFrom":subQ18}),-1.0]])]})]);}
            var Q1;
            Q1=makeQuery(id+"F5.boolean.opBoolean","SPLIT",FACE,{"disambiguationData":[TD([makeQuery(id+"F5.opExtrude","SWEPT_FACE",FACE,{"disambiguationData":[OSD([sQuery(id+"F4.wireOp",EDGE,"E41")])]})])],"derivedFrom":makeQuery(id+"F3.boolean.opBoolean","COPY",FACE,{"derivedFrom":makeQuery(id+"F3.opExtrude","CAP_FACE",FACE,{"disambiguationData":[OSD([sQuery(id+"F0.wireOp",EDGE,"E25.0"),sQuery(id+"F0.wireOp",EDGE,"E25.1"),sQuery(id+"F0.wireOp",EDGE,"E25.2"),sQuery(id+"F0.wireOp",EDGE,"E25.3"),sQuery(id+"F0.wireOp",EDGE,"E25.4"),sQuery(id+"F0.wireOp",EDGE,"E25.5"),sQuery(id+"F0.wireOp",EDGE,"E25.6"),sQuery(id+"F0.wireOp",EDGE,"E25.7")])],"isStart":false})})});
            extrude(context, id + "F13", {"entities" : qUnion([Q0]), "operationType" : NewBodyOperationType.REMOVE, "endBound" : BoundingType.UP_TO_SURFACE, "endBoundEntityFace" : qUnion([Q1]), "depth" : 25 * mm});
        }
        {
            var Q0;
            Q0=makeQuery(id+"F3.boolean.opBoolean","COPY",EDGE,{"derivedFrom":makeQuery(id+"F3.opExtrude","CAP_EDGE",EDGE,{"disambiguationData":[OSD([sQuery(id+"F0.wireOp",EDGE,"E25.6")])],"isStart":false})});
            var Q1;
            Q1=makeQuery(id+"F8.boolean.opBoolean","INTERSECT",EDGE,{"derivedFrom":[makeQuery(id+"F5.opExtrude","SWEPT_FACE",FACE,{"disambiguationData":[OSD([sQuery(id+"F4.wireOp",EDGE,"E30")])]}),makeQuery(id+"F8.opExtrude","CAP_FACE",FACE,{"disambiguationData":[OSD([sQuery(id+"F7.wireOp",EDGE,"E67")])],"isStart":false})]});
            var Q2;
            Q2=makeQuery(id+"F8.boolean.opBoolean","INTERSECT",EDGE,{"disambiguationData":[OD(1.0)],"derivedFrom":[makeQuery(id+"F5.opExtrude","SWEPT_FACE",FACE,{"disambiguationData":[OSD([sQuery(id+"F4.wireOp",EDGE,"E30")])]}),makeQuery(id+"F8.opExtrude","SWEPT_FACE",FACE,{"disambiguationData":[OSD([sQuery(id+"F7.wireOp",EDGE,"E67")])]})]});
            var Q3;
            {var subQ0=sQuery(id+"F4.wireOp",EDGE,"E30");Q3=makeQuery(id+"F8.boolean.opBoolean","SPLIT",EDGE,{"disambiguationData":[TD([makeQuery(id+"F5.opExtrude","SWEPT_FACE",FACE,{"disambiguationData":[OSD([sQuery(id+"F4.wireOp",EDGE,"E35.filletArc")])]})])],"derivedFrom":makeQuery(id+"F5.opExtrude","CAP_EDGE",EDGE,{"disambiguationData":[OSD([subQ0])],"isStart":false})});}
            var Q4;
            {var subQ0=sQuery(id+"F0.wireOp",EDGE,"E25.7");var subQ1=sQuery(id+"F0.wireOp",EDGE,"E25.1");var subQ2=sQuery(id+"F0.wireOp",EDGE,"E25.6");var subQ3=sQuery(id+"F0.wireOp",EDGE,"E25.5");var subQ4=sQuery(id+"F0.wireOp",EDGE,"E25.4");var subQ5=sQuery(id+"F0.wireOp",EDGE,"E25.0");var subQ6=sQuery(id+"F0.wireOp",EDGE,"E25.2");var subQ7=sQuery(id+"F0.wireOp",EDGE,"E25.3");Q4=makeQuery(id+"F8.boolean.opBoolean","INTERSECT",EDGE,{"derivedFrom":[makeQuery(id+"F5.boolean.opBoolean","SPLIT",FACE,{"disambiguationData":[TD([makeQuery(id+"F2.opExtrude","SWEPT_FACE",FACE,{"disambiguationData":[OSD([subQ5])]})])],"derivedFrom":makeQuery(id+"F3.boolean.opBoolean","COPY",FACE,{"derivedFrom":makeQuery(id+"F3.opExtrude","CAP_FACE",FACE,{"disambiguationData":[OSD([subQ5,subQ1,subQ6,subQ7,subQ4,subQ3,subQ2,subQ0])],"isStart":false})})}),makeQuery(id+"F8.opExtrude","SWEPT_FACE",FACE,{"disambiguationData":[OSD([sQuery(id+"F7.wireOp",EDGE,"E67")])]})]});}
            var Q5;
            Q5=makeQuery(id+"F8.boolean.opBoolean","INTERSECT",EDGE,{"disambiguationData":[OD(0.0)],"derivedFrom":[makeQuery(id+"F5.opExtrude","SWEPT_FACE",FACE,{"disambiguationData":[OSD([sQuery(id+"F4.wireOp",EDGE,"E30")])]}),makeQuery(id+"F8.opExtrude","SWEPT_FACE",FACE,{"disambiguationData":[OSD([sQuery(id+"F7.wireOp",EDGE,"E67")])]})]});
            fillet(context, id + "F14", {"entities" : qUnion([Q0, Q1, Q2, Q3, Q4, Q5]), "radius" : 3 * mm, "tangentPropagation" : true, "allowEdgeOverflow" : false});
        }
        {
            var Q0;
            Q0=makeQuery(id+"F1.opExtrude","CAP_EDGE",EDGE,{"disambiguationData":[OSD([sQuery(id+"F0.wireOp",EDGE,"E1.bottom")])],"isStart":false});
            fillet(context, id + "F15", {"entities" : qUnion([Q0]), "radius" : 2 * mm, "tangentPropagation" : true, "allowEdgeOverflow" : false});
        }
        {
            var Q0;
            {var subQ0=sQuery(id+"F0.wireOp",EDGE,"E21.filletArc");var subQ1=sQuery(id+"F0.wireOp",EDGE,"E7");var subQ2=sQuery(id+"F0.wireOp",EDGE,"E6");var subQ3=sQuery(id+"F0.wireOp",EDGE,"E5");var subQ4=sQuery(id+"F0.wireOp",EDGE,"E4");var subQ5=sQuery(id+"F0.wireOp",EDGE,"E22.filletArc");var subQ6=sQuery(id+"F0.wireOp",EDGE,"E1.bottom");var subQ7=sQuery(id+"F0.wireOp",EDGE,"E1.right");var subQ8=sQuery(id+"F0.wireOp",EDGE,"E1.top");var subQ9=sQuery(id+"F0.wireOp",EDGE,"E1.left");var subQ10=sQuery(id+"F0.wireOp",EDGE,"E23.filletArc");var subQ11=sQuery(id+"F0.wireOp",EDGE,"E24.filletArc");Q0=makeQuery(id+"F2.boolean.opBoolean","SPLIT",FACE,{"disambiguationData":[TD([makeQuery(id+"F1.opExtrude","SWEPT_FACE",FACE,{"disambiguationData":[OSD([subQ6])]})])],"derivedFrom":makeQuery(id+"F1.opExtrude","CAP_FACE",FACE,{"disambiguationData":[OSD([subQ6,subQ8,subQ9,subQ7,subQ4,subQ3,subQ2,subQ1,subQ0,subQ5,subQ10,subQ11])],"isStart":true})});}
            var sketch = newSketch(context, id + "F16", { "sketchPlane" : qUnion([Q0])});
            skLineSegment(sketch, "E79", {"start": v(0, 74.25) * mm, "end": v(0, 104.25) * mm, "construction": true});
            skArc(sketch, "E80", {"start": v(15, 104.25) * mm, "mid": v(0, 119.25) * mm, "end": v(-15, 104.25) * mm});
            skLineSegment(sketch, "E81", {"start": v(15, 104.25) * mm, "end": v(15, 92.25) * mm});
            skLineSegment(sketch, "E82", {"start": v(-15, 104.25) * mm, "end": v(-15, 92.25) * mm});
            skLineSegment(sketch, "E83", {"start": v(15, 92.25) * mm, "end": v(33, 74.25) * mm});
            skLineSegment(sketch, "E84", {"start": v(-15, 92.25) * mm, "end": v(-33, 74.25) * mm});
            skCircle(sketch, "E85", {"center": v(0, 104.25) * mm, "radius": 6 * mm});
            skLineSegment(sketch, "E86", {"start": v(-74.25, 0) * mm, "end": v(74.25, 0) * mm, "construction": true});
            skLineSegment(sketch, "E87.MirrorCS", {"start": v(0, -74.25) * mm, "end": v(0, -104.25) * mm, "construction": true});
            skArc(sketch, "E88.MirrorCS", {"start": v(15, -104.25) * mm, "mid": v(0, -119.25) * mm, "end": v(-15, -104.25) * mm});
            skLineSegment(sketch, "E89.MirrorCS", {"start": v(15, -104.25) * mm, "end": v(15, -92.25) * mm});
            skLineSegment(sketch, "E90.MirrorCS", {"start": v(-15, -104.25) * mm, "end": v(-15, -92.25) * mm});
            skLineSegment(sketch, "E91.MirrorCS", {"start": v(15, -92.25) * mm, "end": v(33, -74.25) * mm});
            skCircle(sketch, "E92.MirrorC", {"center": v(0, -104.25) * mm, "radius": 6 * mm});
            skLineSegment(sketch, "E93.MirrorCS", {"start": v(-15, -92.25) * mm, "end": v(-33, -74.25) * mm});
            skSolve(sketch);
        }
        {
            var Q0;
            Q0=makeQuery(id+"F16.imprint","IMPRINT",FACE,{"disambiguationData":[TD([[makeQuery(id+"F16.imprint","IMPRINT",EDGE,{"derivedFrom":sQuery(id+"F16.wireOp",EDGE,"E80")}),1.0]])]});
            var Q1;
            Q1=makeQuery(id+"F16.imprint","IMPRINT",FACE,{"disambiguationData":[TD([[makeQuery(id+"F16.imprint","IMPRINT",EDGE,{"derivedFrom":makeQuery(id+"F1.opExtrude","CAP_EDGE",EDGE,{"disambiguationData":[OSD([sQuery(id+"F0.wireOp",EDGE,"E1.left")])],"isStart":true})}),-1.0]])]});
            var Q2;
            Q2=makeQuery(id+"F16.imprint","IMPRINT",FACE,{"disambiguationData":[TD([[makeQuery(id+"F16.imprint","IMPRINT",EDGE,{"derivedFrom":sQuery(id+"F16.wireOp",EDGE,"E88.MirrorCS")}),-1.0]])]});
            var Q3;
            Q3=makeQuery(id+"F2.opExtrude","CAP_FACE",FACE,{"disambiguationData":[OSD([sQuery(id+"F0.wireOp",EDGE,"E12"),sQuery(id+"F0.wireOp",EDGE,"E13"),sQuery(id+"F0.wireOp",EDGE,"E14"),sQuery(id+"F0.wireOp",EDGE,"E15"),sQuery(id+"F0.wireOp",EDGE,"E17.filletArc"),sQuery(id+"F0.wireOp",EDGE,"E18.filletArc"),sQuery(id+"F0.wireOp",EDGE,"E19.filletArc"),sQuery(id+"F0.wireOp",EDGE,"E20.filletArc"),sQuery(id+"F0.wireOp",EDGE,"E25.0"),sQuery(id+"F0.wireOp",EDGE,"E25.1"),sQuery(id+"F0.wireOp",EDGE,"E25.2"),sQuery(id+"F0.wireOp",EDGE,"E25.3"),sQuery(id+"F0.wireOp",EDGE,"E25.4"),sQuery(id+"F0.wireOp",EDGE,"E25.5"),sQuery(id+"F0.wireOp",EDGE,"E25.6"),sQuery(id+"F0.wireOp",EDGE,"E25.7")])],"isStart":false});
            extrude(context, id + "F17", {"entities" : qUnion([Q0, Q1, Q2]), "endBound" : BoundingType.UP_TO_SURFACE, "endBoundEntityFace" : qUnion([Q3]), "depth" : 25 * mm});
        }
    });
